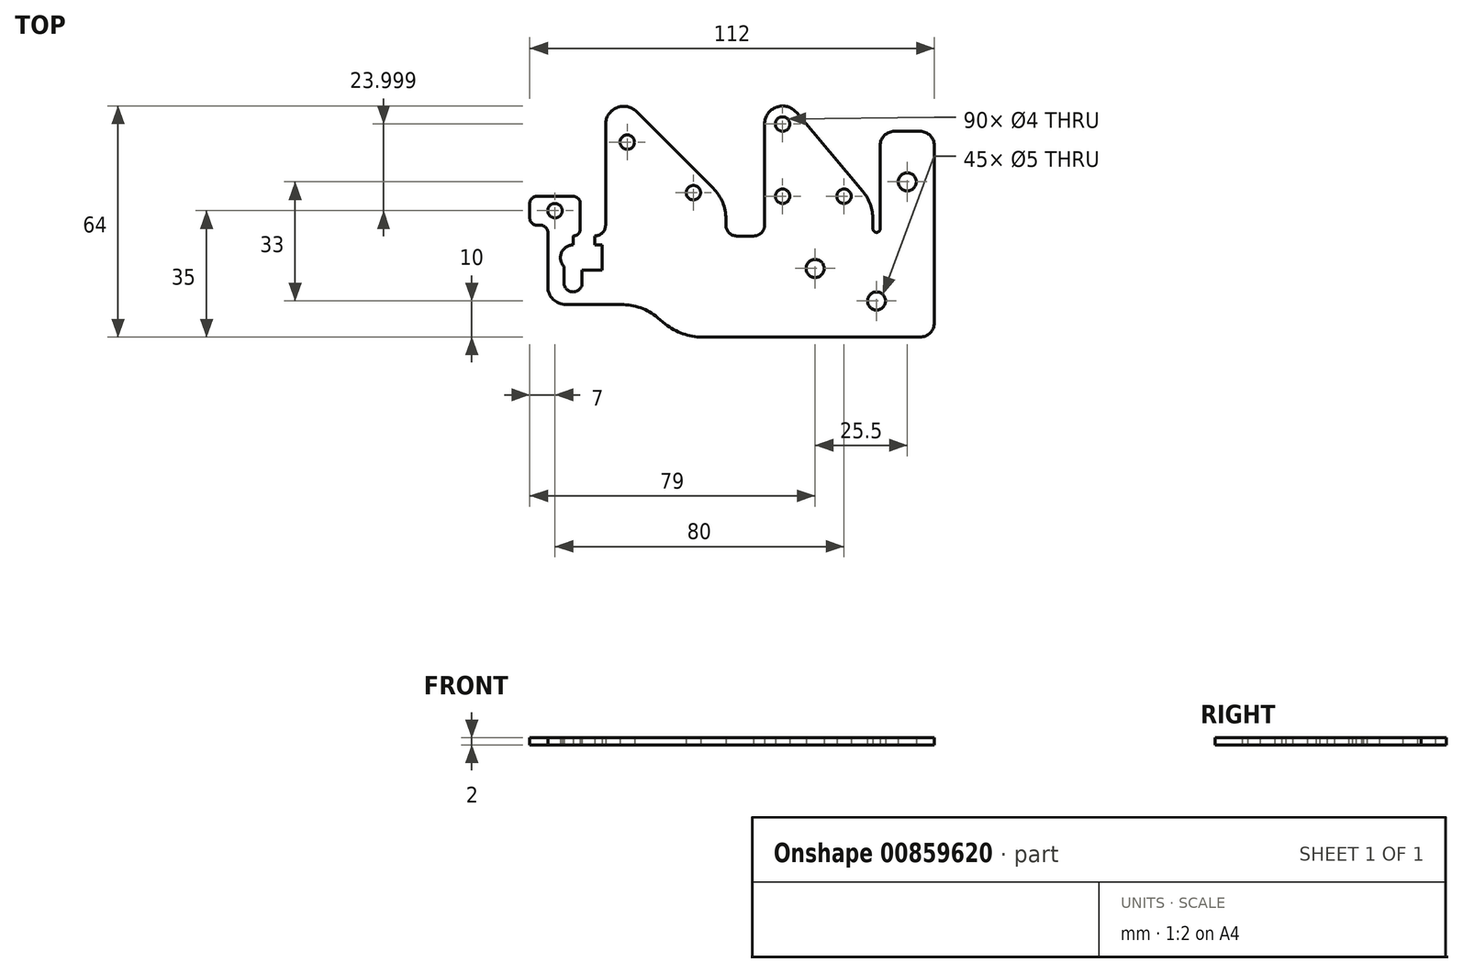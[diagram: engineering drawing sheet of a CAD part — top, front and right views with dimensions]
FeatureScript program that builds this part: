
annotation { "Feature Type Name" : "Feature", "Feature Type Description" : "" }
export const myFeature = defineFeature(function(context is Context, id is Id, definition is map)
    precondition{}
    {
        {
            var Q0;
            Q0=qCreatedBy(makeId("Top.planeOp"),FACE);
            var sketch = newSketch(context, id + "F0", { "sketchPlane" : qUnion([Q0])});
            skLineSegment(sketch, "E0.bottom", {"start": v(26, 28.5) * mm, "end": v(-26, 28.5) * mm});
            skLineSegment(sketch, "E0.top", {"start": v(26, -28.5) * mm, "end": v(-26, -28.5) * mm});
            skLineSegment(sketch, "E0.left", {"start": v(26, 28.5) * mm, "end": v(26, -28.5) * mm});
            skLineSegment(sketch, "E0.right", {"start": v(-26, 28.5) * mm, "end": v(-26, 2.5) * mm});
            skPoint(sketch, "E0.middle", {"position": v(0, 0) * mm});
            skLineSegment(sketch, "E1", {"start": v(26, 28.5) * mm, "end": v(11, 28.5) * mm});
            skLineSegment(sketch, "E2", {"start": v(11, 28.5) * mm, "end": v(11, 1.5) * mm});
            skLineSegment(sketch, "E3", {"start": v(11, -28.5) * mm, "end": v(9, -28.5) * mm});
            skLineSegment(sketch, "E4.right", {"start": v(-26, -28.5) * mm, "end": v(-26, 2.5) * mm});
            skLineSegment(sketch, "E5.left", {"start": v(9, 2.5) * mm, "end": v(9, 1.5) * mm});
            skLineSegment(sketch, "E5.right", {"start": v(11, 2.5) * mm, "end": v(11, 1.5) * mm});
            skArc(sketch, "E6", {"start": v(9, 1.5) * mm, "mid": v(10, 0.5) * mm, "end": v(11, 1.5) * mm});
            skArc(sketch, "E7", {"start": v(15, 28.5) * mm, "mid": v(12.17, 27.33) * mm, "end": v(11, 24.5) * mm});
            skArc(sketch, "E8", {"start": v(26, 24.5) * mm, "mid": v(24.83, 27.33) * mm, "end": v(22, 28.5) * mm});
            skLineSegment(sketch, "E9.trimOffspring", {"start": v(9, 1.5) * mm, "end": v(9, 2.5) * mm});
            skLineSegment(sketch, "E10.top", {"start": v(-21, 10.5) * mm, "end": v(-18, 10.5) * mm});
            skLineSegment(sketch, "E10.left", {"start": v(-21, 2.5) * mm, "end": v(-21, 10.5) * mm});
            skCircle(sketch, "E11", {"center": v(-16, 10.5) * mm, "radius": 2 * mm});
            skCircle(sketch, "E12", {"center": v(-16, 30.5) * mm, "radius": 2 * mm});
            skLineSegment(sketch, "E13", {"start": v(-21, 2.5) * mm, "end": v(-21, 30.5) * mm});
            skArc(sketch, "E14", {"start": v(-12.17, 33.71) * mm, "mid": v(-17.71, 35.2) * mm, "end": v(-21, 30.5) * mm});
            skLineSegment(sketch, "E15.trimOffspring", {"start": v(9, 8.48) * mm, "end": v(-12.17, 33.71) * mm});
            skLineSegment(sketch, "E16", {"start": v(9, 2.5) * mm, "end": v(9, 8.48) * mm});
            skLineSegment(sketch, "E17", {"start": v(-14, 10.5) * mm, "end": v(1, 10.5) * mm});
            skCircle(sketch, "E18", {"center": v(1, 10.5) * mm, "radius": 2 * mm});
            skLineSegment(sketch, "E19.bottom", {"start": v(26, -28.5) * mm, "end": v(22, -28.5) * mm});
            skLineSegment(sketch, "E19.left", {"start": v(26, -28.5) * mm, "end": v(26, -24.5) * mm});
            skArc(sketch, "E20", {"start": v(22, -28.5) * mm, "mid": v(24.83, -27.33) * mm, "end": v(26, -24.5) * mm});
            skLineSegment(sketch, "E21.bottom", {"start": v(-26, -28.5) * mm, "end": v(-44, -28.5) * mm});
            skLineSegment(sketch, "E21.top", {"start": v(-26, 2.5) * mm, "end": v(-68, 2.5) * mm});
            skLineSegment(sketch, "E21.right", {"start": v(-68, -19.5) * mm, "end": v(-68, 2.5) * mm});
            skLineSegment(sketch, "E22.top", {"start": v(-68, -19.5) * mm, "end": v(-81, -19.5) * mm});
            skLineSegment(sketch, "E22.left", {"start": v(-68, 2.5) * mm, "end": v(-68, -19.5) * mm});
            skLineSegment(sketch, "E23.top", {"start": v(-72, 10.5) * mm, "end": v(-86, 10.5) * mm});
            skLineSegment(sketch, "E23.left", {"start": v(-72, -0.5) * mm, "end": v(-72, 10.5) * mm});
            skLineSegment(sketch, "E23.right", {"start": v(-86, 2.5) * mm, "end": v(-86, 10.5) * mm});
            skLineSegment(sketch, "E24.bottom", {"start": v(26, -28.5) * mm, "end": v(-7, -28.5) * mm});
            skCircle(sketch, "E25", {"center": v(-7, -9.5) * mm, "radius": 2.5 * mm});
            skLineSegment(sketch, "E26", {"start": v(10, -28.5) * mm, "end": v(10, -18.5) * mm});
            skCircle(sketch, "E27", {"center": v(10, -18.5) * mm, "radius": 2.5 * mm});
            skLineSegment(sketch, "E28", {"start": v(18.5, 28.5) * mm, "end": v(18.5, 14.5) * mm});
            skCircle(sketch, "E29", {"center": v(18.5, 14.5) * mm, "radius": 2.5 * mm});
            skLineSegment(sketch, "E30", {"start": v(-68, -19.5) * mm, "end": v(-55, -19.5) * mm});
            skLineSegment(sketch, "E31", {"start": v(-55, -19.5) * mm, "end": v(-44, -28.5) * mm});
            skLineSegment(sketch, "E32", {"start": v(-81, -19.5) * mm, "end": v(-81, -0.5) * mm});
            skLineSegment(sketch, "E33", {"start": v(-81, -0.5) * mm, "end": v(-68, -0.5) * mm});
            skArc(sketch, "E34", {"start": v(-24.08, -0.5) * mm, "mid": v(-21.9, 0.35) * mm, "end": v(-21, 2.5) * mm});
            skLineSegment(sketch, "E35", {"start": v(-23.92, -0.5) * mm, "end": v(-26, -0.5) * mm});
            skLineSegment(sketch, "E36", {"start": v(-26, -0.5) * mm, "end": v(-28.7, -0.5) * mm});
            skArc(sketch, "E37", {"start": v(-31.7, 2.5) * mm, "mid": v(-30.82, 0.38) * mm, "end": v(-28.7, -0.5) * mm});
            skLineSegment(sketch, "E38.trimOffspring", {"start": v(-26, -0.5) * mm, "end": v(-26, -28.5) * mm});
            skArc(sketch, "E39", {"start": v(-68, -0.5) * mm, "mid": v(-65.88, 0.38) * mm, "end": v(-65, 2.5) * mm});
            skLineSegment(sketch, "E40", {"start": v(-65, 2.5) * mm, "end": v(-65, 34.5) * mm});
            skLineSegment(sketch, "E41", {"start": v(-31.7, 9.2) * mm, "end": v(-65, 42.5) * mm});
            skLineSegment(sketch, "E42", {"start": v(-65, 34.5) * mm, "end": v(-65, 42.5) * mm});
            skLineSegment(sketch, "E43", {"start": v(-31.7, 2.5) * mm, "end": v(-31.7, 9.2) * mm});
            skLineSegment(sketch, "E44.bottom", {"start": v(-31.7, 2.5) * mm, "end": v(-40.7, 2.5) * mm});
            skCircle(sketch, "E45", {"center": v(-40.7, 11.5) * mm, "radius": 2 * mm});
            skCircle(sketch, "E46", {"center": v(-59, 25.5) * mm, "radius": 2 * mm});
            skCircle(sketch, "E47", {"center": v(-74, -13.5) * mm, "radius": 2.5 * mm});
            skLineSegment(sketch, "E48", {"start": v(-81, -0.5) * mm, "end": v(-74, -0.5) * mm});
            skLineSegment(sketch, "E49", {"start": v(-74, -0.5) * mm, "end": v(-74, -6.5) * mm});
            skCircle(sketch, "E50", {"center": v(-74, -6.5) * mm, "radius": 3.5 * mm});
            skLineSegment(sketch, "E51", {"start": v(-76.5, -13.5) * mm, "end": v(-76.5, -8.95) * mm});
            skLineSegment(sketch, "E52", {"start": v(-71.5, -13.5) * mm, "end": v(-71.5, -8.95) * mm});
            skLineSegment(sketch, "E53", {"start": v(-74, -3) * mm, "end": v(-66, -3) * mm});
            skLineSegment(sketch, "E54", {"start": v(-74, -10) * mm, "end": v(-66, -10) * mm});
            skLineSegment(sketch, "E55", {"start": v(-66, -10) * mm, "end": v(-66, -3) * mm});
            skLineSegment(sketch, "E56.top", {"start": v(-81, 2.5) * mm, "end": v(-86, 2.5) * mm});
            skLineSegment(sketch, "E56.left", {"start": v(-81, -0.5) * mm, "end": v(-81, 2.5) * mm});
            skCircle(sketch, "E57", {"center": v(-79, 6.5) * mm, "radius": 2 * mm});
            skPoint(sketch, "E57.centerSnap0", {"position": v(-79, 10.5) * mm});
            skPoint(sketch, "E57.centerSnap1", {"position": v(-86, 6.5) * mm});
            skSolve(sketch);
        }
        {
            var Q0;
            {var subQ0=sQuery(id+"F0.wireOp",EDGE,"E40");Q0=makeQuery(id+"F0.imprint","IMPRINT",FACE,{"disambiguationData":[TD([[makeQuery(id+"F0.imprint","IMPRINT",EDGE,{"derivedFrom":subQ0}),-1.0]])]});}
            var Q1;
            Q1=makeQuery(id+"F0.imprint","IMPRINT",FACE,{"disambiguationData":[TD([[makeQuery(id+"F0.imprint","IMPRINT",EDGE,{"derivedFrom":sQuery(id+"F0.wireOp",EDGE,"E21.bottom")}),-1.0]])]});
            var Q2;
            {var subQ2=sQuery(id+"F0.wireOp",EDGE,"E22.left");var subQ6=sQuery(id+"F0.wireOp",EDGE,"E53");var subQ8=makeQuery(id+"F0.imprint","INTERSECT",VERTEX,{"derivedFrom":[subQ2,subQ6]});Q2=makeQuery(id+"F0.imprint","IMPRINT",FACE,{"disambiguationData":[TD([[makeQuery(id+"F0.imprint","IMPRINT",EDGE,{"disambiguationData":[TD([[subQ8,1.0]])],"derivedFrom":subQ2}),-1.0]])]});}
            var Q3;
            {var subQ8=sQuery(id+"F0.wireOp",EDGE,"E22.top");Q3=makeQuery(id+"F0.imprint","IMPRINT",FACE,{"disambiguationData":[TD([[makeQuery(id+"F0.imprint","IMPRINT",EDGE,{"derivedFrom":subQ8}),-1.0]])]});}
            var Q4;
            Q4=makeQuery(id+"F0.imprint","IMPRINT",FACE,{"disambiguationData":[TD([[makeQuery(id+"F0.imprint","IMPRINT",EDGE,{"derivedFrom":sQuery(id+"F0.wireOp",EDGE,"E23.top")}),1.0]])]});
            var Q5;
            {var subQ16=sQuery(id+"F0.wireOp",EDGE,"E0.top");Q5=makeQuery(id+"F0.imprint","IMPRINT",FACE,{"disambiguationData":[TD([[makeQuery(id+"F0.imprint","IMPRINT",EDGE,{"derivedFrom":subQ16}),-1.0]])]});}
            var Q6;
            {var subQ8=sQuery(id+"F0.wireOp",EDGE,"E14");Q6=makeQuery(id+"F0.imprint","IMPRINT",FACE,{"disambiguationData":[TD([[makeQuery(id+"F0.imprint","IMPRINT",EDGE,{"derivedFrom":subQ8}),1.0]])]});}
            extrude(context, id + "F1", {"entities" : qUnion([Q0, Q1, Q2, Q3, Q4, Q5, Q6]), "depth" : 2 * mm, "offsetDistance" : 25 * mm});
        }
        {
            var Q0;
            Q0=makeQuery(id+"F1.opExtrude","SWEPT_EDGE",EDGE,{"disambiguationData":[OSD([sQuery(id+"F0.wireOp",EDGE,"E23.top"),sQuery(id+"F0.wireOp",EDGE,"E23.left")])]});
            var Q1;
            Q1=makeQuery(id+"F1.opExtrude","SWEPT_EDGE",EDGE,{"disambiguationData":[OSD([sQuery(id+"F0.wireOp",EDGE,"E23.top"),sQuery(id+"F0.wireOp",EDGE,"E23.right")])]});
            var Q2;
            Q2=makeQuery(id+"F1.opExtrude","SWEPT_EDGE",EDGE,{"disambiguationData":[OSD([sQuery(id+"F0.wireOp",EDGE,"E23.right"),sQuery(id+"F0.wireOp",EDGE,"E56.top")])]});
            var Q3;
            Q3=makeQuery(id+"F1.opExtrude","SWEPT_EDGE",EDGE,{"disambiguationData":[OSD([sQuery(id+"F0.wireOp",EDGE,"E56.top"),sQuery(id+"F0.wireOp",EDGE,"E56.left")])]});
            var Q4;
            Q4=makeQuery(id+"F1.opExtrude","SWEPT_EDGE",EDGE,{"disambiguationData":[OSD([sQuery(id+"F0.wireOp",EDGE,"E23.left"),sQuery(id+"F0.wireOp",EDGE,"E33")])]});
            fillet(context, id + "F2", {"entities" : qUnion([Q0, Q1, Q2, Q3, Q4]), "radius" : 2 * mm, "tangentPropagation" : true, "allowEdgeOverflow" : false});
        }
        {
            var Q0;
            Q0=makeQuery(id+"F1.opExtrude","SWEPT_EDGE",EDGE,{"disambiguationData":[OSD([sQuery(id+"F0.wireOp",EDGE,"E41"),sQuery(id+"F0.wireOp",EDGE,"E42")])]});
            fillet(context, id + "F3", {"entities" : qUnion([Q0]), "radius" : 5 * mm, "tangentPropagation" : true, "allowEdgeOverflow" : false});
        }
        {
            var Q0;
            Q0=makeQuery(id+"F1.opExtrude","SWEPT_EDGE",EDGE,{"disambiguationData":[OSD([sQuery(id+"F0.wireOp",EDGE,"E41"),sQuery(id+"F0.wireOp",EDGE,"E43")])]});
            var Q1;
            Q1=makeQuery(id+"F1.opExtrude","SWEPT_EDGE",EDGE,{"disambiguationData":[OSD([sQuery(id+"F0.wireOp",EDGE,"E15.trimOffspring"),sQuery(id+"F0.wireOp",EDGE,"E16")])]});
            fillet(context, id + "F4", {"entities" : qUnion([Q0, Q1]), "radius" : 12 * mm, "tangentPropagation" : true, "allowEdgeOverflow" : false});
        }
        {
            var Q0;
            Q0=makeQuery(id+"F1.opExtrude","SWEPT_EDGE",EDGE,{"disambiguationData":[OSD([sQuery(id+"F0.wireOp",EDGE,"E22.top"),sQuery(id+"F0.wireOp",EDGE,"E32")])]});
            fillet(context, id + "F5", {"entities" : qUnion([Q0]), "radius" : 5 * mm, "tangentPropagation" : true, "allowEdgeOverflow" : false});
        }
        {
            var Q0;
            Q0=makeQuery(id+"F1.opExtrude","SWEPT_EDGE",EDGE,{"disambiguationData":[OSD([sQuery(id+"F0.wireOp",EDGE,"E30"),sQuery(id+"F0.wireOp",EDGE,"E31")])]});
            var Q1;
            Q1=makeQuery(id+"F1.opExtrude","SWEPT_EDGE",EDGE,{"disambiguationData":[OSD([sQuery(id+"F0.wireOp",EDGE,"E21.bottom"),sQuery(id+"F0.wireOp",EDGE,"E31")])]});
            fillet(context, id + "F6", {"entities" : qUnion([Q0, Q1]), "radius" : 16 * mm, "tangentPropagation" : true, "allowEdgeOverflow" : false});
        }
    });
